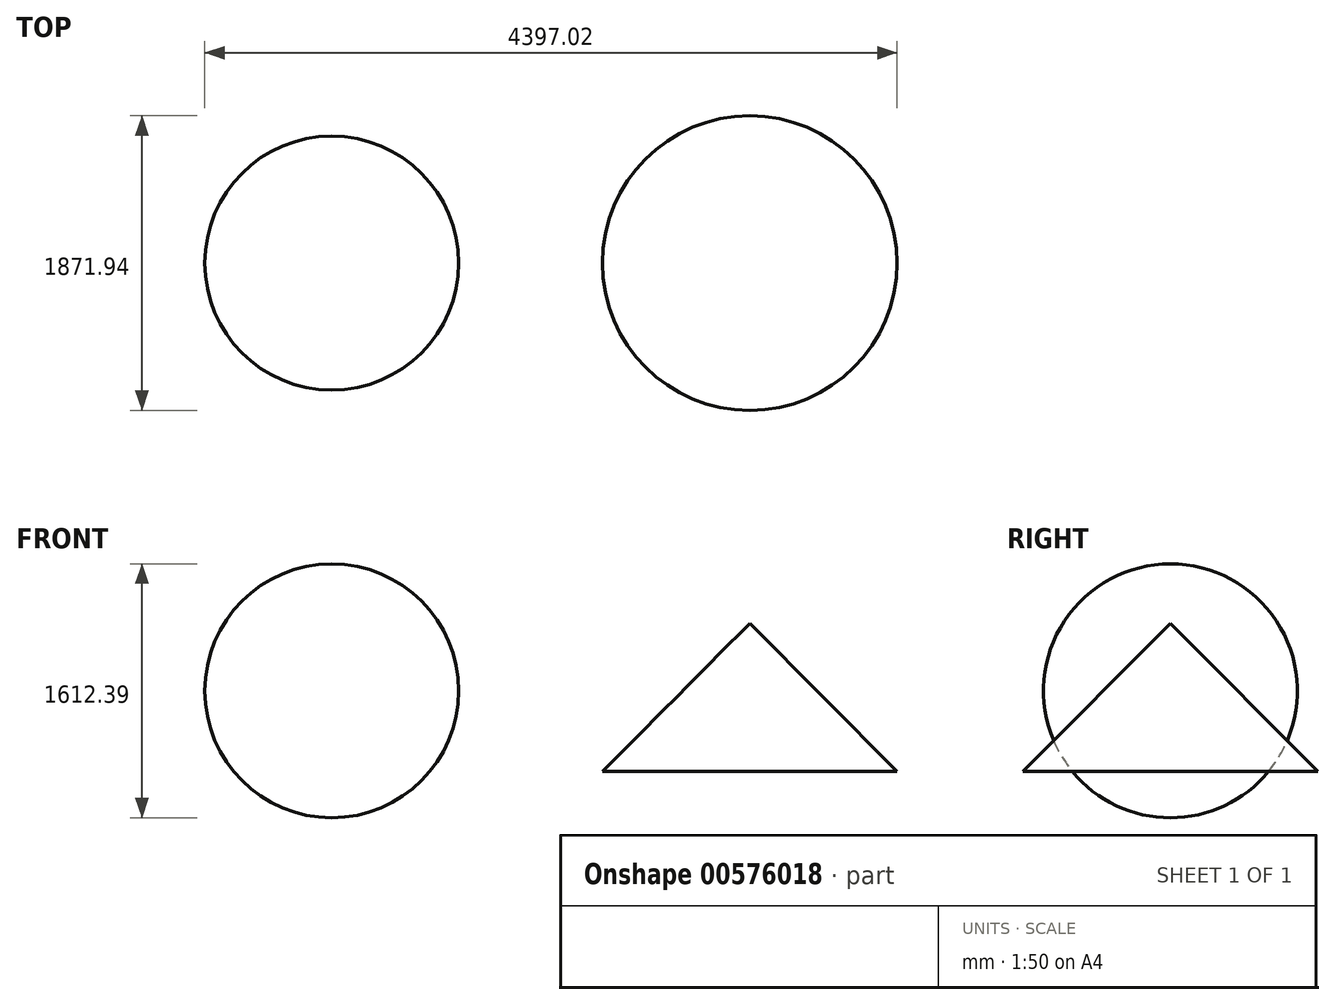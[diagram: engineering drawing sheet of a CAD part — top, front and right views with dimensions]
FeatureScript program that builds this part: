
annotation { "Feature Type Name" : "Feature", "Feature Type Description" : "" }
export const myFeature = defineFeature(function(context is Context, id is Id, definition is map)
    precondition{}
    {
        {
            var Q0;
            Q0=qCreatedBy(makeId("Front.planeOp"),FACE);
            var sketch = newSketch(context, id + "F0", { "sketchPlane" : qUnion([Q0])});
            skLineSegment(sketch, "E0", {"start": v(-379.13, -179.2) * mm, "end": v(556.84, -179.2) * mm});
            skLineSegment(sketch, "E1", {"start": v(-379.13, -179.2) * mm, "end": v(-379.13, 762.7) * mm});
            skLineSegment(sketch, "E2", {"start": v(-379.13, 762.7) * mm, "end": v(556.84, -179.2) * mm});
            skSolve(sketch);
        }
        {
            var Q0;
            Q0=makeQuery(id+"F0.imprint","IMPRINT",FACE,{"disambiguationData":[TD([[makeQuery(id+"F0.imprint","IMPRINT",EDGE,{"derivedFrom":sQuery(id+"F0.wireOp",EDGE,"E0")}),1.0]])]});
            var Q1;
            Q1=sQuery(id+"F0.wireOp",EDGE,"E1");
            revolve(context, id + "F1", {"entities" : qUnion([Q0]), "axis" : qUnion([Q1]), "revolveType" : RevolveType.FULL});
        }
        {
            var Q0;
            Q0=qCreatedBy(makeId("Front.planeOp"),FACE);
            var sketch = newSketch(context, id + "F2", { "sketchPlane" : qUnion([Q0])});
            skCircle(sketch, "E3", {"center": v(-3033.98, 333.63) * mm, "radius": 806.2 * mm});
            skLineSegment(sketch, "E4", {"start": v(-3033.98, 333.63) * mm, "end": v(-3033.98, -472.56) * mm});
            skLineSegment(sketch, "E5", {"start": v(-3033.98, -472.56) * mm, "end": v(-3033.98, 1139.83) * mm});
            skSolve(sketch);
        }
        {
            var Q0;
            {var subQ0=sQuery(id+"F2.wireOp",EDGE,"E5");var subQ4=makeQuery(id+"F2.imprint","IMPRINT",VERTEX,{"derivedFrom":subQ0});Q0=makeQuery(id+"F2.imprint","IMPRINT",FACE,{"disambiguationData":[TD([[makeQuery(id+"F2.imprint","IMPRINT",EDGE,{"disambiguationData":[TD([[subQ4,1.0]])],"derivedFrom":subQ0}),1.0]])]});}
            var Q1;
            Q1=sQuery(id+"F2.wireOp",EDGE,"E5");
            revolve(context, id + "F3", {"entities" : qUnion([Q0]), "axis" : qUnion([Q1]), "revolveType" : RevolveType.FULL});
        }
    });
